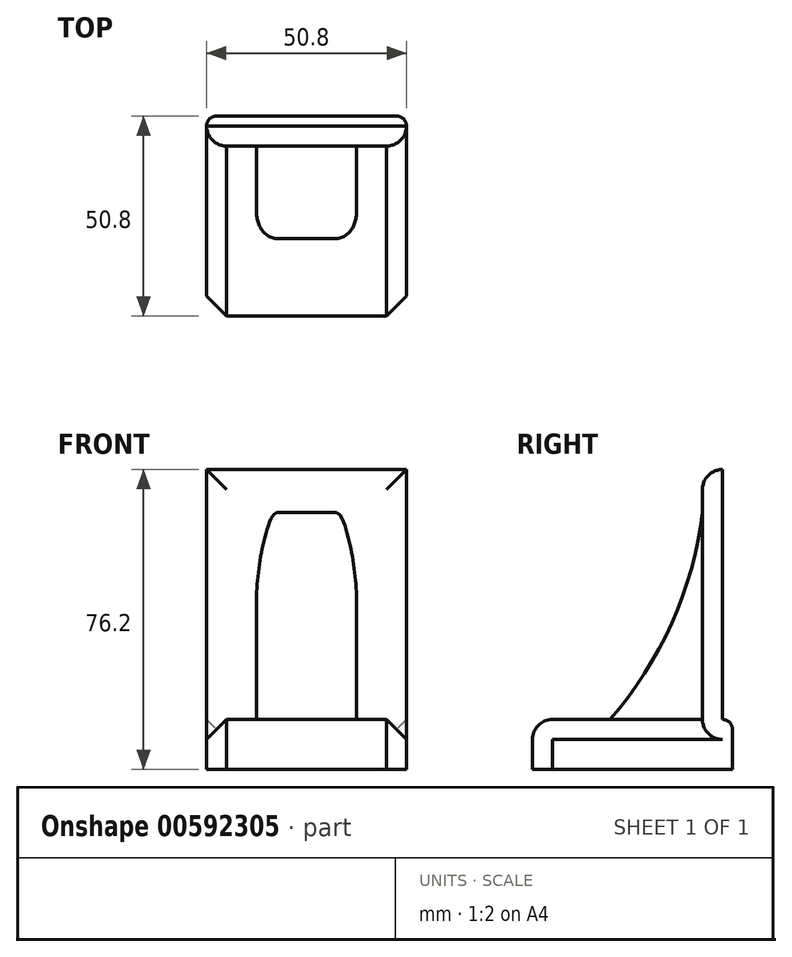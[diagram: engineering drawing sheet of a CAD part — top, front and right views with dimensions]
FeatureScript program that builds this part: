
annotation { "Feature Type Name" : "Feature", "Feature Type Description" : "" }
export const myFeature = defineFeature(function(context is Context, id is Id, definition is map)
    precondition{}
    {
        {
            var Q0;
            Q0=qCreatedBy(makeId("Top.planeOp"),FACE);
            var sketch = newSketch(context, id + "F0", { "sketchPlane" : qUnion([Q0])});
            skLineSegment(sketch, "E0.bottom", {"start": v(-25.4, 7.62) * mm, "end": v(0, 7.62) * mm});
            skLineSegment(sketch, "E0.top", {"start": v(-25.4, -43.18) * mm, "end": v(0, -43.18) * mm});
            skLineSegment(sketch, "E0.left", {"start": v(-25.4, 7.62) * mm, "end": v(-25.4, -43.18) * mm});
            skLineSegment(sketch, "E1.MirrorCS", {"start": v(25.4, 7.62) * mm, "end": v(25.4, -43.18) * mm});
            skLineSegment(sketch, "E2.MirrorCS", {"start": v(25.4, 7.62) * mm, "end": v(0, 7.62) * mm});
            skLineSegment(sketch, "E3.MirrorCS", {"start": v(25.4, -43.18) * mm, "end": v(0, -43.18) * mm});
            skSolve(sketch);
        }
        {
            var Q0;
            Q0=makeQuery(id+"F0.imprint","IMPRINT",FACE,{"disambiguationData":[TD([[makeQuery(id+"F0.imprint","IMPRINT",EDGE,{"derivedFrom":sQuery(id+"F0.wireOp",EDGE,"E0.bottom")}),-1.0]])]});
            extrude(context, id + "F1", {"entities" : qUnion([Q0]), "oppositeDirection" : true, "depth" : 12.7 * mm, "offsetDistance" : 25.4 * mm});
        }
        {
            var Q0;
            Q0=qCreatedBy(makeId("Front.planeOp"),FACE);
            var sketch = newSketch(context, id + "F2", { "sketchPlane" : qUnion([Q0])});
            skLineSegment(sketch, "E4.bottom", {"start": v(0, 0) * mm, "end": v(-25.4, 0) * mm});
            skLineSegment(sketch, "E4.top", {"start": v(0, 63.5) * mm, "end": v(-25.4, 63.5) * mm});
            skLineSegment(sketch, "E4.right", {"start": v(-25.4, 0) * mm, "end": v(-25.4, 63.5) * mm});
            skLineSegment(sketch, "E5.MirrorCS", {"start": v(25.4, 0) * mm, "end": v(25.4, 63.5) * mm});
            skLineSegment(sketch, "E6.MirrorCS", {"start": v(0, 63.5) * mm, "end": v(25.4, 63.5) * mm});
            skLineSegment(sketch, "E7.MirrorCS", {"start": v(0, 0) * mm, "end": v(25.4, 0) * mm});
            skSolve(sketch);
        }
        {
            var Q0;
            Q0=makeQuery(id+"F2.imprint","IMPRINT",FACE,{"disambiguationData":[TD([[makeQuery(id+"F2.imprint","IMPRINT",EDGE,{"derivedFrom":sQuery(id+"F2.wireOp",EDGE,"E4.bottom")}),-1.0]])]});
            extrude(context, id + "F3", {"entities" : qUnion([Q0]), "operationType" : NewBodyOperationType.ADD, "oppositeDirection" : true, "depth" : 5.08 * mm, "offsetDistance" : 25.4 * mm});
        }
        {
            var Q0;
            Q0=qCreatedBy(makeId("Right.planeOp"),FACE);
            var sketch = newSketch(context, id + "F4", { "sketchPlane" : qUnion([Q0])});
            skArc(sketch, "E8", {"start": v(-23.46, 0) * mm, "mid": v(-7.78, 24.5) * mm, "end": v(0, 52.52) * mm});
            skLineSegment(sketch, "E9", {"start": v(0, 52.52) * mm, "end": v(0, 0) * mm});
            skLineSegment(sketch, "E10", {"start": v(0, 0) * mm, "end": v(-23.46, 0) * mm});
            skSolve(sketch);
        }
        {
            var Q0;
            Q0=makeQuery(id+"F4.imprint","IMPRINT",FACE,{"disambiguationData":[TD([[makeQuery(id+"F4.imprint","IMPRINT",EDGE,{"derivedFrom":sQuery(id+"F4.wireOp",EDGE,"E8")}),-1.0]])]});
            extrude(context, id + "F5", {"entities" : qUnion([Q0]), "operationType" : NewBodyOperationType.ADD, "depth" : 12.7 * mm, "offsetDistance" : 25.4 * mm, "hasSecondDirection" : true, "secondDirectionOppositeDirection" : true, "secondDirectionDepth" : 12.7 * mm});
        }
        {
            var Q0;
            Q0=makeQuery(id+"F3.opExtrude","CAP_EDGE",EDGE,{"disambiguationData":[OSD([sQuery(id+"F2.wireOp",EDGE,"E4.top"),sQuery(id+"F2.wireOp",EDGE,"E6.MirrorCS")])],"isStart":true});
            var Q1;
            Q1=makeQuery(id+"F3.opExtrude","CAP_EDGE",EDGE,{"disambiguationData":[OSD([sQuery(id+"F2.wireOp",EDGE,"E4.right")])],"isStart":true});
            var Q2;
            Q2=makeQuery(id+"F3.opExtrude","CAP_EDGE",EDGE,{"disambiguationData":[OSD([sQuery(id+"F2.wireOp",EDGE,"E5.MirrorCS")])],"isStart":true});
            fillet(context, id + "F6", {"entities" : qUnion([Q0, Q1, Q2]), "radius" : 5.08 * mm, "tangentPropagation" : true, "allowEdgeOverflow" : false});
        }
        {
            var Q0;
            Q0=makeQuery(id+"F1.opExtrude","CAP_EDGE",EDGE,{"disambiguationData":[OSD([sQuery(id+"F0.wireOp",EDGE,"E0.top"),sQuery(id+"F0.wireOp",EDGE,"E3.MirrorCS")])],"isStart":true});
            fillet(context, id + "F7", {"entities" : qUnion([Q0]), "radius" : 5.08 * mm, "tangentPropagation" : true, "allowEdgeOverflow" : false});
        }
        {
            var Q0;
            {var subQ1=sQuery(id+"F0.wireOp",EDGE,"E3.MirrorCS");var subQ2=sQuery(id+"F0.wireOp",EDGE,"E0.top");var subQ3=sQuery(id+"F0.wireOp",EDGE,"E1.MirrorCS");Q0=makeQuery(id+"F3.boolean.opBoolean","SPLIT",EDGE,{"disambiguationData":[TD([makeQuery(id+"F1.opExtrude","SWEPT_FACE",FACE,{"disambiguationData":[OSD([subQ2,subQ1])]})])],"derivedFrom":makeQuery(id+"F1.opExtrude","CAP_EDGE",EDGE,{"disambiguationData":[OSD([subQ3])],"isStart":true})});}
            var Q1;
            {var subQ0=sQuery(id+"F0.wireOp",EDGE,"E0.left");var subQ2=sQuery(id+"F0.wireOp",EDGE,"E3.MirrorCS");var subQ3=sQuery(id+"F0.wireOp",EDGE,"E0.top");Q1=makeQuery(id+"F3.boolean.opBoolean","SPLIT",EDGE,{"disambiguationData":[TD([makeQuery(id+"F1.opExtrude","SWEPT_FACE",FACE,{"disambiguationData":[OSD([subQ3,subQ2])]})])],"derivedFrom":makeQuery(id+"F1.opExtrude","CAP_EDGE",EDGE,{"disambiguationData":[OSD([subQ0])],"isStart":true})});}
            chamfer(context, id + "F8", {"entities" : qUnion([Q0, Q1]), "width" : 5.08 * mm, "tangentPropagation" : true});
        }
        {
            var Q0;
            Q0=makeQuery(id+"F5.opExtrude","CAP_EDGE",EDGE,{"disambiguationData":[OSD([sQuery(id+"F4.wireOp",EDGE,"E8")])],"isStart":false});
            var Q1;
            Q1=makeQuery(id+"F5.opExtrude","CAP_EDGE",EDGE,{"disambiguationData":[OSD([sQuery(id+"F4.wireOp",EDGE,"E8")])],"isStart":true});
            fillet(context, id + "F9", {"entities" : qUnion([Q0, Q1]), "radius" : 5.08 * mm, "tangentPropagation" : true, "allowEdgeOverflow" : false});
        }
        {
            var Q0;
            Q0=makeQuery(id+"F1.opExtrude","CAP_EDGE",EDGE,{"disambiguationData":[OSD([sQuery(id+"F0.wireOp",EDGE,"E0.bottom"),sQuery(id+"F0.wireOp",EDGE,"E2.MirrorCS")])],"isStart":true});
            var Q1;
            Q1=makeQuery(id+"F1.opExtrude","SWEPT_EDGE",EDGE,{"disambiguationData":[OSD([sQuery(id+"F0.wireOp",EDGE,"E0.bottom"),sQuery(id+"F0.wireOp",EDGE,"E0.left")])]});
            var Q2;
            Q2=makeQuery(id+"F1.opExtrude","SWEPT_EDGE",EDGE,{"disambiguationData":[OSD([sQuery(id+"F0.wireOp",EDGE,"E1.MirrorCS"),sQuery(id+"F0.wireOp",EDGE,"E2.MirrorCS")])]});
            fillet(context, id + "F10", {"entities" : qUnion([Q0, Q1, Q2]), "radius" : 2.54 * mm, "tangentPropagation" : true, "allowEdgeOverflow" : false});
        }
    });
